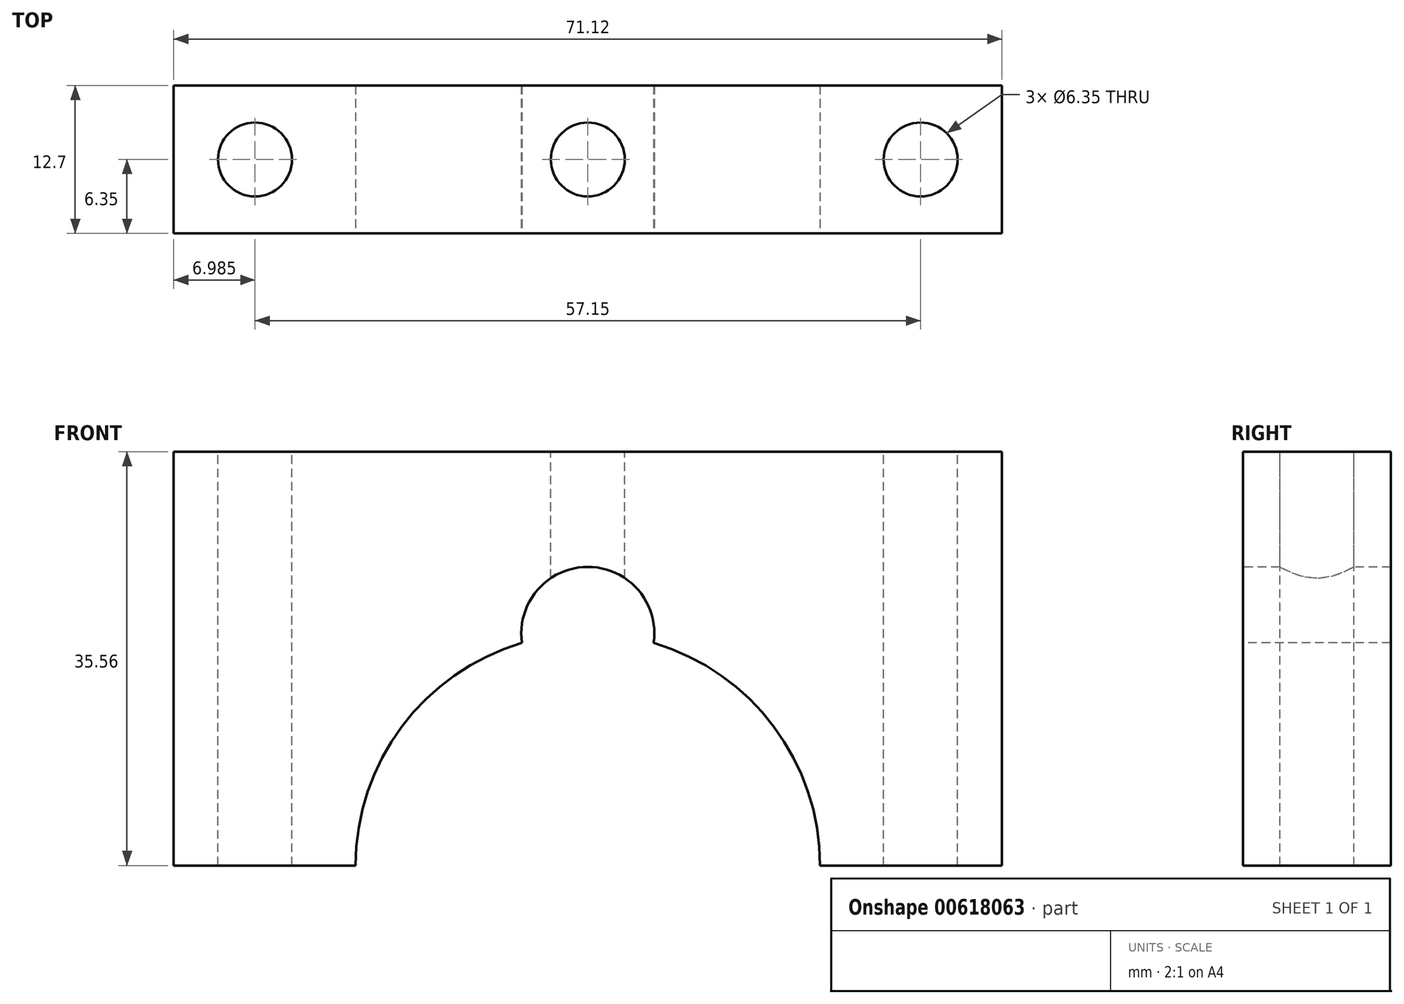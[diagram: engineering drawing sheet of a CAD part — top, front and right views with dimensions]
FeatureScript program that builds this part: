
annotation { "Feature Type Name" : "Feature", "Feature Type Description" : "" }
export const myFeature = defineFeature(function(context is Context, id is Id, definition is map)
    precondition{}
    {
        {
            var Q0;
            Q0=qCreatedBy(makeId("Front.planeOp"),FACE);
            var sketch = newSketch(context, id + "F0", { "sketchPlane" : qUnion([Q0])});
            skLineSegment(sketch, "E0.bottom", {"start": v(35.56, 17.78) * mm, "end": v(-35.56, 17.78) * mm});
            skLineSegment(sketch, "E0.top", {"start": v(35.56, -17.78) * mm, "end": v(-35.56, -17.78) * mm});
            skLineSegment(sketch, "E0.left", {"start": v(35.56, 17.78) * mm, "end": v(35.56, -17.78) * mm});
            skLineSegment(sketch, "E0.right", {"start": v(-35.56, 17.78) * mm, "end": v(-35.56, -17.78) * mm});
            skPoint(sketch, "E0.middle", {"position": v(0, 0) * mm});
            skSolve(sketch);
        }
        {
            var Q0;
            Q0=makeQuery(id+"F0.imprint","IMPRINT",FACE,{"disambiguationData":[TD([[makeQuery(id+"F0.imprint","IMPRINT",EDGE,{"derivedFrom":sQuery(id+"F0.wireOp",EDGE,"E0.bottom")}),1.0]])]});
            extrude(context, id + "F1", {"entities" : qUnion([Q0]), "depth" : 12.7 * mm, "offsetDistance" : 25.4 * mm});
        }
        {
            var Q0;
            Q0=makeQuery(id+"F1.opExtrude","CAP_FACE",FACE,{"disambiguationData":[OSD([sQuery(id+"F0.wireOp",EDGE,"E0.bottom"),sQuery(id+"F0.wireOp",EDGE,"E0.top"),sQuery(id+"F0.wireOp",EDGE,"E0.left"),sQuery(id+"F0.wireOp",EDGE,"E0.right")])],"isStart":false});
            var sketch = newSketch(context, id + "F2", { "sketchPlane" : qUnion([Q0])});
            skCircle(sketch, "E1", {"center": v(0, -17.78) * mm, "radius": 19.94 * mm});
            skSolve(sketch);
        }
        {
            var Q0;
            {var subQ0=sQuery(id+"F2.wireOp",EDGE,"E1");var subQ1=makeQuery(id+"F1.opExtrude","CAP_EDGE",EDGE,{"disambiguationData":[OSD([sQuery(id+"F0.wireOp",EDGE,"E0.top")])],"isStart":false});var subQ2=makeQuery(id+"F2.imprint","INTERSECT",VERTEX,{"disambiguationData":[OD(0.0)],"derivedFrom":[subQ1,subQ0]});Q0=makeQuery(id+"F2.imprint","IMPRINT",FACE,{"disambiguationData":[TD([[makeQuery(id+"F2.imprint","IMPRINT",EDGE,{"disambiguationData":[TD([[subQ2,-1.0]])],"derivedFrom":subQ0}),1.0]])]});}
            extrude(context, id + "F3", {"entities" : qUnion([Q0]), "operationType" : NewBodyOperationType.REMOVE, "endBound" : BoundingType.THROUGH_ALL, "oppositeDirection" : true, "depth" : 25.4 * mm, "offsetDistance" : 25.4 * mm});
        }
        {
            var Q0;
            Q0=makeQuery(id+"F1.opExtrude","CAP_FACE",FACE,{"disambiguationData":[OSD([sQuery(id+"F0.wireOp",EDGE,"E0.bottom"),sQuery(id+"F0.wireOp",EDGE,"E0.top"),sQuery(id+"F0.wireOp",EDGE,"E0.left"),sQuery(id+"F0.wireOp",EDGE,"E0.right")])],"isStart":false});
            var sketch = newSketch(context, id + "F4", { "sketchPlane" : qUnion([Q0])});
            skCircle(sketch, "E2", {"center": v(0, 2.16) * mm, "radius": 5.72 * mm});
            skSolve(sketch);
        }
        {
            var Q0;
            {var subQ0=sQuery(id+"F4.wireOp",EDGE,"E2");var subQ1=makeQuery(id+"F3.boolean.opBoolean","COPY",EDGE,{"derivedFrom":makeQuery(id+"F3.opExtrude","CAP_EDGE",EDGE,{"disambiguationData":[OSD([sQuery(id+"F2.wireOp",EDGE,"E1")])],"isStart":true})});var subQ2=makeQuery(id+"F4.imprint","INTERSECT",VERTEX,{"disambiguationData":[OD(0.0)],"derivedFrom":[subQ1,subQ0]});Q0=makeQuery(id+"F4.imprint","IMPRINT",FACE,{"disambiguationData":[TD([[makeQuery(id+"F4.imprint","IMPRINT",EDGE,{"disambiguationData":[TD([[subQ2,-1.0]])],"derivedFrom":subQ0}),1.0]])]});}
            extrude(context, id + "F5", {"entities" : qUnion([Q0]), "operationType" : NewBodyOperationType.REMOVE, "oppositeDirection" : true, "depth" : 25.4 * mm, "offsetDistance" : 25.4 * mm});
        }
        {
            var Q0;
            Q0=makeQuery(id+"F1.opExtrude","SWEPT_FACE",FACE,{"disambiguationData":[OSD([sQuery(id+"F0.wireOp",EDGE,"E0.bottom")])]});
            var sketch = newSketch(context, id + "F6", { "sketchPlane" : qUnion([Q0])});
            skCircle(sketch, "E3", {"center": v(-28.57, -6.35) * mm, "radius": 3.18 * mm});
            skPoint(sketch, "E3.centerSnap0", {"position": v(-35.56, -6.35) * mm});
            skCircle(sketch, "E4", {"center": v(0, -6.35) * mm, "radius": 3.18 * mm});
            skCircle(sketch, "E5", {"center": v(28.57, -6.35) * mm, "radius": 3.18 * mm});
            skSolve(sketch);
        }
        {
            var Q0;
            Q0=sQuery(id+"F6.wireOp",VERTEX,"E3.center");
            var Q1;
            Q1=sQuery(id+"F6.wireOp",VERTEX,"E4.center");
            var Q2;
            Q2=sQuery(id+"F6.wireOp",VERTEX,"E5.center");
            var Q3;
            Q3=makeQuery(id+"F1.opExtrude","SWEPT_BODY",BODY,{"disambiguationData":[OSD([sQuery(id+"F0.wireOp",EDGE,"E0.bottom"),sQuery(id+"F0.wireOp",EDGE,"E0.top"),sQuery(id+"F0.wireOp",EDGE,"E0.left"),sQuery(id+"F0.wireOp",EDGE,"E0.right")])]});
            hole(context, id + "F7", {"style" : HoleStyle.SIMPLE, "endStyle" : HoleEndStyle.BLIND, "holeDiameter" : 6.35 * mm, "majorDiameter" : 6.35 * mm, "holeDepth" : 50.8 * mm, "isTappedThrough" : true, "tappedDepth" : 12.7 * mm, "tapClearance" : 3, "startFromSketch" : true, "locations" : qUnion([Q0, Q1, Q2]), "scope" : qUnion([Q3])});
        }
    });
